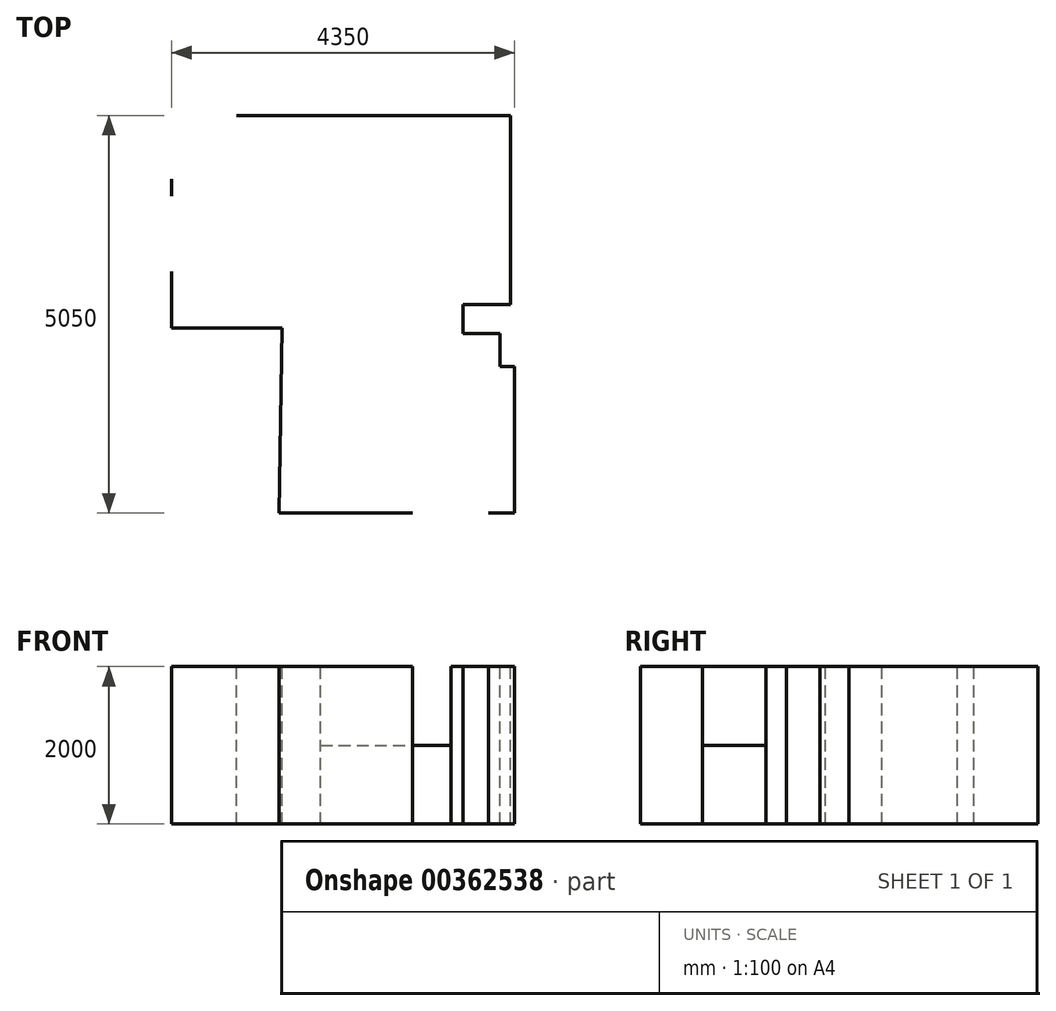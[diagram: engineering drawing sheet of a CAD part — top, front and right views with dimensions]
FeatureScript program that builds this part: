
annotation { "Feature Type Name" : "Feature", "Feature Type Description" : "" }
export const myFeature = defineFeature(function(context is Context, id is Id, definition is map)
    precondition{}
    {
        {
            var Q0;
            Q0=qCreatedBy(makeId("Top.planeOp"),FACE);
            var sketch = newSketch(context, id + "F0", { "sketchPlane" : qUnion([Q0])});
            skLineSegment(sketch, "E0", {"start": v(-1399.4, 0) * mm, "end": v(0, 0) * mm});
            skLineSegment(sketch, "E1", {"start": v(0, 0) * mm, "end": v(-39.4, -2350) * mm});
            skLineSegment(sketch, "E2", {"start": v(2950.6, -490) * mm, "end": v(2770.6, -490) * mm});
            skLineSegment(sketch, "E3", {"start": v(2770.6, -490) * mm, "end": v(2770.6, -70) * mm});
            skLineSegment(sketch, "E4", {"start": v(2900.6, 300) * mm, "end": v(2900.6, 2700) * mm});
            skPoint(sketch, "E5", {"position": v(-1399.4, 2700) * mm});
            skPoint(sketch, "E6", {"position": v(-579.4, 2700) * mm});
            skPoint(sketch, "E7", {"position": v(490.6, 2700) * mm});
            skPoint(sketch, "E8", {"position": v(2150.6, 2700) * mm});
            skPoint(sketch, "E9", {"position": v(-1399.4, 1890) * mm});
            skPoint(sketch, "E10", {"position": v(-1399.4, 1680) * mm});
            skPoint(sketch, "E11", {"position": v(-1399.4, 720) * mm});
            skLineSegment(sketch, "E12", {"start": v(2900.6, 300) * mm, "end": v(2300.6, 300) * mm});
            skLineSegment(sketch, "E13", {"start": v(2300.6, -70) * mm, "end": v(2300.6, 300) * mm});
            skLineSegment(sketch, "E14", {"start": v(2300.6, -70) * mm, "end": v(2770.6, -70) * mm});
            skLineSegment(sketch, "E15", {"start": v(2950.6, -490) * mm, "end": v(2950.6, -750) * mm});
            skLineSegment(sketch, "E16", {"start": v(-579.4, 2700) * mm, "end": v(490.6, 2700) * mm});
            skLineSegment(sketch, "E17", {"start": v(2150.6, 2700) * mm, "end": v(2900.6, 2700) * mm});
            skLineSegment(sketch, "E18", {"start": v(-1399.4, 1890) * mm, "end": v(-1399.4, 1680) * mm});
            skLineSegment(sketch, "E19", {"start": v(-1399.4, 720) * mm, "end": v(-1399.4, 0) * mm});
            skLineSegment(sketch, "E20", {"start": v(2950.6, -1560) * mm, "end": v(2950.6, -2350) * mm});
            skLineSegment(sketch, "E21", {"start": v(2950.6, -2350) * mm, "end": v(2620.6, -2350) * mm});
            skPoint(sketch, "E22", {"position": v(1660.6, -2350) * mm});
            skLineSegment(sketch, "E23", {"start": v(1660.6, -2350) * mm, "end": v(-39.4, -2350) * mm});
            skLineSegment(sketch, "E24", {"start": v(490.6, 2700) * mm, "end": v(2150.6, 2700) * mm});
            skLineSegment(sketch, "E25", {"start": v(-1399.4, 2700) * mm, "end": v(-579.4, 2700) * mm});
            skLineSegment(sketch, "E26", {"start": v(-1399.4, 2700) * mm, "end": v(-1399.4, 1890) * mm});
            skLineSegment(sketch, "E27", {"start": v(-1399.4, 1680) * mm, "end": v(-1399.4, 720) * mm});
            skLineSegment(sketch, "E28", {"start": v(2950.6, -750) * mm, "end": v(2950.6, -1560) * mm});
            skLineSegment(sketch, "E29", {"start": v(2620.6, -2350) * mm, "end": v(1660.6, -2350) * mm});
            skLineSegment(sketch, "E30", {"start": v(-1399.4, 720) * mm, "end": v(-663.97, 1337.04) * mm});
            skArc(sketch, "E31", {"start": v(-1399.4, 1680) * mm, "mid": v(-993.67, 1590.05) * mm, "end": v(-663.97, 1337.04) * mm});
            skArc(sketch, "E32", {"start": v(1660.6, -2350) * mm, "mid": v(1707.47, -2646.3) * mm, "end": v(1843.5, -2913.67) * mm});
            skLineSegment(sketch, "E33", {"start": v(2620.6, -2350) * mm, "end": v(1843.5, -2913.67) * mm});
            skArc(sketch, "E34", {"start": v(-1399.4, 1890) * mm, "mid": v(-1130.47, 1935.95) * mm, "end": v(-892.05, 2068.58) * mm});
            skLineSegment(sketch, "E35", {"start": v(-1399.4, 2700) * mm, "end": v(-892.05, 2068.58) * mm});
            skSolve(sketch);
        }
        {
            var Q0;
            Q0=makeQuery(id+"F0.imprint","IMPRINT",FACE,{"disambiguationData":[TD([[makeQuery(id+"F0.imprint","IMPRINT",EDGE,{"derivedFrom":sQuery(id+"F0.wireOp",EDGE,"E0")}),1.0]])]});
            var Q1;
            Q1=sQuery(id+"F0.wireOp",EDGE,"E17");
            var Q2;
            Q2=sQuery(id+"F0.wireOp",EDGE,"E4");
            var Q3;
            Q3=sQuery(id+"F0.wireOp",EDGE,"E12");
            var Q4;
            Q4=sQuery(id+"F0.wireOp",EDGE,"E13");
            var Q5;
            Q5=sQuery(id+"F0.wireOp",EDGE,"E14");
            var Q6;
            Q6=sQuery(id+"F0.wireOp",EDGE,"E3");
            var Q7;
            Q7=sQuery(id+"F0.wireOp",EDGE,"E2");
            var Q8;
            Q8=sQuery(id+"F0.wireOp",EDGE,"E15");
            var Q9;
            Q9=sQuery(id+"F0.wireOp",EDGE,"E20");
            var Q10;
            Q10=sQuery(id+"F0.wireOp",EDGE,"E21");
            var Q11;
            Q11=sQuery(id+"F0.wireOp",EDGE,"E23");
            var Q12;
            Q12=sQuery(id+"F0.wireOp",EDGE,"E1");
            var Q13;
            Q13=sQuery(id+"F0.wireOp",EDGE,"E0");
            var Q14;
            Q14=sQuery(id+"F0.wireOp",EDGE,"E19");
            var Q15;
            Q15=sQuery(id+"F0.wireOp",EDGE,"E18");
            var Q16;
            Q16=sQuery(id+"F0.wireOp",EDGE,"E16");
            extrude(context, id + "F1", {"entities" : qUnion([Q0]), "bodyType" : ToolBodyType.SURFACE, "surfaceEntities" : qUnion([Q1, Q2, Q3, Q4, Q5, Q6, Q7, Q8, Q9, Q10, Q11, Q12, Q13, Q14, Q15, Q16]), "depth" : 2000 * mm});
        }
        {
            var Q0;
            Q0=sQuery(id+"F0.wireOp",EDGE,"E24");
            var Q1;
            Q1=sQuery(id+"F0.wireOp",EDGE,"E28");
            extrude(context, id + "F2", {"bodyType" : ToolBodyType.SURFACE, "surfaceEntities" : qUnion([Q0, Q1]), "depth" : 1000 * mm});
        }
    });
